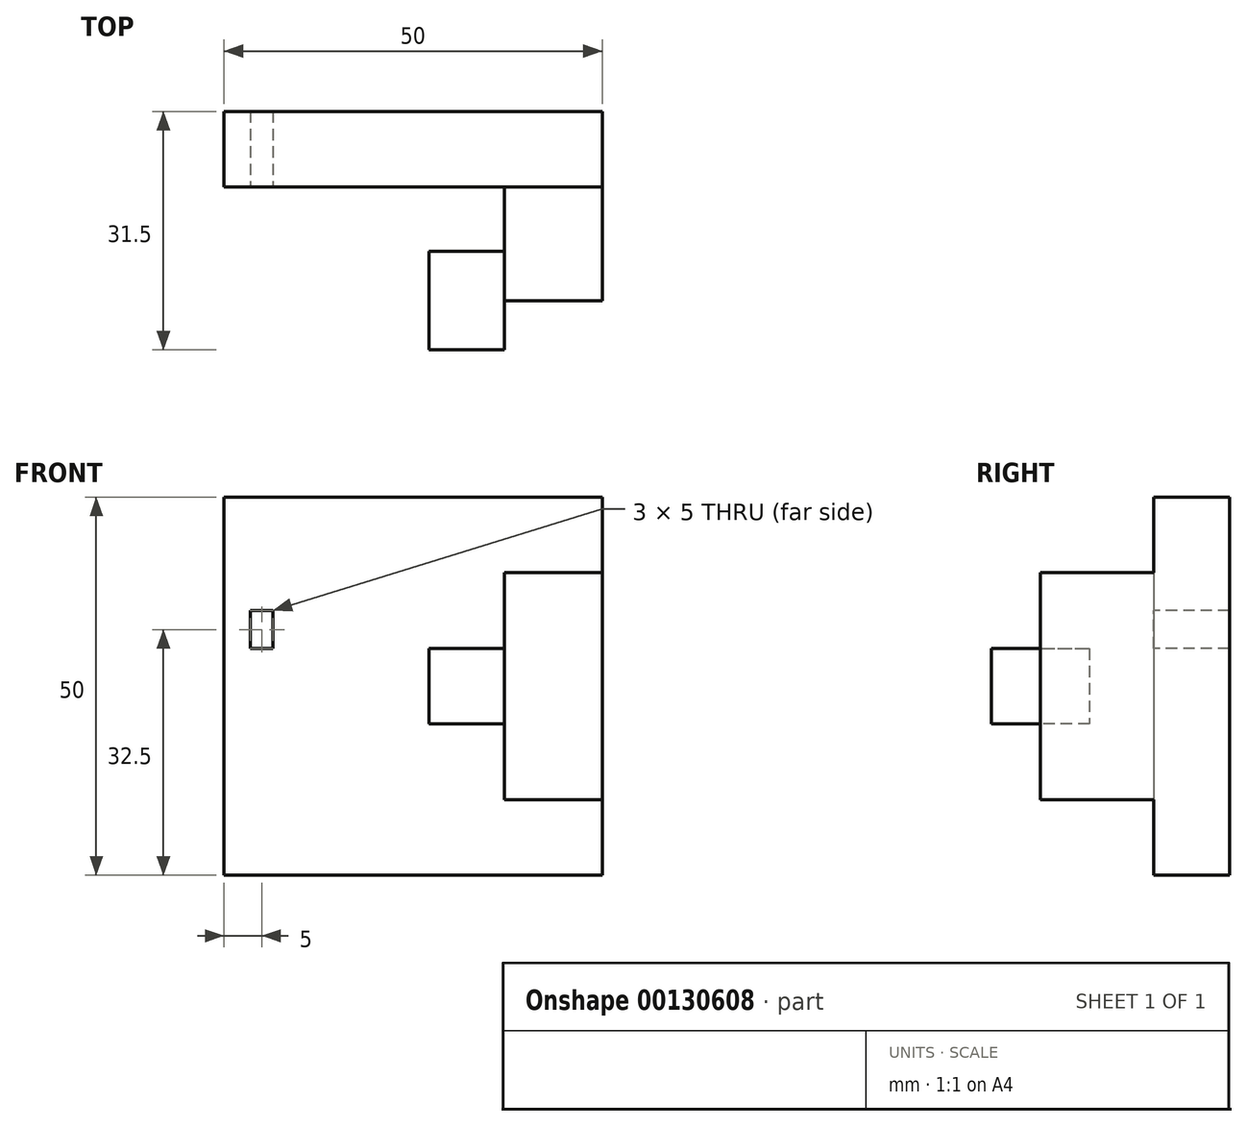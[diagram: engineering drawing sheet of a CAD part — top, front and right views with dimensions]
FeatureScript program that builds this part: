
annotation { "Feature Type Name" : "Feature", "Feature Type Description" : "" }
export const myFeature = defineFeature(function(context is Context, id is Id, definition is map)
    precondition{}
    {
        {
            var Q0;
            Q0=qCreatedBy(makeId("Front.planeOp"),FACE);
            var sketch = newSketch(context, id + "F0", { "sketchPlane" : qUnion([Q0])});
            skLineSegment(sketch, "E0.bottom", {"start": v(25, 25) * mm, "end": v(-25, 25) * mm});
            skLineSegment(sketch, "E0.top", {"start": v(25, -25) * mm, "end": v(-25, -25) * mm});
            skLineSegment(sketch, "E0.left", {"start": v(25, 25) * mm, "end": v(25, -25) * mm});
            skLineSegment(sketch, "E0.right", {"start": v(-25, 25) * mm, "end": v(-25, -25) * mm});
            skPoint(sketch, "E0.middle", {"position": v(0, 0) * mm});
            skLineSegment(sketch, "E1", {"start": v(25, 15) * mm, "end": v(12.1, 15) * mm});
            skLineSegment(sketch, "E2", {"start": v(12.1, 15) * mm, "end": v(12.1, -15) * mm});
            skLineSegment(sketch, "E3", {"start": v(12.1, -15) * mm, "end": v(25, -15) * mm});
            skLineSegment(sketch, "E4", {"start": v(-25, -15) * mm, "end": v(-12.1, -15) * mm});
            skLineSegment(sketch, "E5", {"start": v(-12.1, -15) * mm, "end": v(-12.1, 15) * mm});
            skLineSegment(sketch, "E6", {"start": v(-12.1, 15) * mm, "end": v(-25, 15) * mm});
            skSolve(sketch);
        }
        {
            var Q0;
            {var subQ0=sQuery(id+"F0.wireOp",EDGE,"E1");Q0=makeQuery(id+"F0.imprint","IMPRINT",FACE,{"disambiguationData":[TD([[makeQuery(id+"F0.imprint","IMPRINT",EDGE,{"derivedFrom":subQ0}),1.0]])]});}
            var Q1;
            {var subQ0=sQuery(id+"F0.wireOp",EDGE,"E4");Q1=makeQuery(id+"F0.imprint","IMPRINT",FACE,{"disambiguationData":[TD([[makeQuery(id+"F0.imprint","IMPRINT",EDGE,{"derivedFrom":subQ0}),1.0]])]});}
            extrude(context, id + "F1", {"entities" : qUnion([Q0, Q1]), "depth" : 25 * mm});
        }
        {
            var Q0;
            {var subQ4=sQuery(id+"F0.wireOp",EDGE,"E0.bottom");Q0=makeQuery(id+"F0.imprint","IMPRINT",FACE,{"disambiguationData":[TD([[makeQuery(id+"F0.imprint","IMPRINT",EDGE,{"derivedFrom":subQ4}),1.0]])]});}
            extrude(context, id + "F2", {"entities" : qUnion([Q0]), "operationType" : NewBodyOperationType.ADD, "depth" : 10 * mm});
        }
        {
            var Q0;
            Q0=makeQuery(id+"F1.opExtrude","SWEPT_FACE",FACE,{"disambiguationData":[OSD([sQuery(id+"F0.wireOp",EDGE,"E5")])]});
            var sketch = newSketch(context, id + "F3", { "sketchPlane" : qUnion([Q0])});
            skLineSegment(sketch, "E7", {"start": v(-25, 5) * mm, "end": v(-18.5, 5) * mm});
            skLineSegment(sketch, "E8", {"start": v(-18.5, 5) * mm, "end": v(-18.5, -5) * mm});
            skLineSegment(sketch, "E9", {"start": v(-18.5, -5) * mm, "end": v(-25, -5) * mm});
            skLineSegment(sketch, "E10", {"start": v(-10, 12.16) * mm, "end": v(-10, 1.89) * mm});
            skSolve(sketch);
        }
        {
            var Q0;
            Q0=qSketchRegion(id+"F3",true);
            var Q1;
            {var subQ0=sQuery(id+"F3.wireOp",EDGE,"E7");Q1=makeQuery(id+"F3.imprint","IMPRINT",FACE,{"disambiguationData":[TD([[makeQuery(id+"F3.imprint","IMPRINT",EDGE,{"derivedFrom":subQ0}),-1.0]])]});}
            extrude(context, id + "F4", {"entities" : qUnion([Q0, Q1]), "operationType" : NewBodyOperationType.ADD, "depth" : 10 * mm});
        }
        {
            var Q0;
            Q0=makeQuery(id+"F1.opExtrude","SWEPT_FACE",FACE,{"disambiguationData":[OSD([sQuery(id+"F0.wireOp",EDGE,"E2")])]});
            var sketch = newSketch(context, id + "F5", { "sketchPlane" : qUnion([Q0])});
            skLineSegment(sketch, "E11", {"start": v(25, 5) * mm, "end": v(18.5, 5) * mm});
            skLineSegment(sketch, "E12", {"start": v(18.5, 5) * mm, "end": v(18.5, -5) * mm});
            skLineSegment(sketch, "E13", {"start": v(18.5, -5) * mm, "end": v(25, -5) * mm});
            skSolve(sketch);
        }
        {
            var Q0;
            Q0=qSketchRegion(id+"F5",true);
            var Q1;
            {var subQ0=sQuery(id+"F5.wireOp",EDGE,"E11");Q1=makeQuery(id+"F5.imprint","IMPRINT",FACE,{"disambiguationData":[TD([[makeQuery(id+"F5.imprint","IMPRINT",EDGE,{"derivedFrom":subQ0}),1.0]])]});}
            extrude(context, id + "F6", {"entities" : qUnion([Q0, Q1]), "operationType" : NewBodyOperationType.ADD, "depth" : 10 * mm});
        }
        {
            var Q0;
            {var subQ0=sQuery(id+"F0.wireOp",EDGE,"E0.right");Q0=makeQuery(id+"F2.boolean.opBoolean","MERGE",FACE,{"derivedFrom":[makeQuery(id+"F1.opExtrude","SWEPT_FACE",FACE,{"disambiguationData":[OSD([subQ0])]}),makeQuery(id+"F2.opExtrude","SWEPT_FACE",FACE,{"disambiguationData":[OSD([subQ0]),TDD([makeQuery(id+"F0.imprint","IMPRINT",EDGE,{"disambiguationData":[TD([[makeQuery(id+"F0.imprint","INTERSECT",VERTEX,{"derivedFrom":[sQuery(id+"F0.wireOp",EDGE,"E0.bottom"),subQ0]}),-1.0]])],"derivedFrom":subQ0})])]}),makeQuery(id+"F2.opExtrude","SWEPT_FACE",FACE,{"disambiguationData":[OSD([subQ0]),TDD([makeQuery(id+"F0.imprint","IMPRINT",EDGE,{"disambiguationData":[TD([[makeQuery(id+"F0.imprint","INTERSECT",VERTEX,{"derivedFrom":[sQuery(id+"F0.wireOp",EDGE,"E0.top"),subQ0]}),1.0]])],"derivedFrom":subQ0})])]})]});}
            var sketch = newSketch(context, id + "F7", { "sketchPlane" : qUnion([Q0])});
            skLineSegment(sketch, "E14", {"start": v(10, 15) * mm, "end": v(10, -15) * mm});
            skSolve(sketch);
        }
        {
            var Q0;
            Q0 = qSketchRegion(id + "F7", true);
            var Q1;
            Q1=makeQuery(id+"F7.imprint","IMPRINT",FACE,{"disambiguationData":[TD([[makeQuery(id+"F7.imprint","IMPRINT",EDGE,{"derivedFrom":sQuery(id+"F7.wireOp",EDGE,"E14")}),1.0]])]});
            var Q2;
            Q2=makeQuery(id+"F4.opExtrude","CAP_FACE",FACE,{"disambiguationData":[OSD([sQuery(id+"F0.wireOp",EDGE,"E5"),sQuery(id+"F3.wireOp",EDGE,"E7"),sQuery(id+"F3.wireOp",EDGE,"E8"),sQuery(id+"F3.wireOp",EDGE,"E9")])],"isStart":false});
            extrude(context, id + "F8", {"entities" : qUnion([Q0, Q1]), "operationType" : NewBodyOperationType.REMOVE, "endBound" : BoundingType.UP_TO_SURFACE, "oppositeDirection" : true, "endBoundEntityFace" : qUnion([Q2]), "depth" : 25 * mm});
        }
        {
            var Q0;
            {var subQ0=sQuery(id+"F0.wireOp",EDGE,"E2");Q0=makeQuery(id+"F6.boolean.opBoolean","MERGE",FACE,{"derivedFrom":[makeQuery(id+"F1.opExtrude","CAP_FACE",FACE,{"disambiguationData":[OSD([sQuery(id+"F0.wireOp",EDGE,"E0.left"),sQuery(id+"F0.wireOp",EDGE,"E1"),subQ0,sQuery(id+"F0.wireOp",EDGE,"E3")])],"isStart":false}),makeQuery(id+"F6.opExtrude","SWEPT_FACE",FACE,{"disambiguationData":[OSD([subQ0])]})]});}
            var sketch = newSketch(context, id + "F9", { "sketchPlane" : qUnion([Q0])});
            skLineSegment(sketch, "E15", {"start": v(12.1, 5) * mm, "end": v(12.1, -5) * mm});
            skSolve(sketch);
        }
        {
            var Q0;
            Q0 = qSketchRegion(id + "F9", true);
            var Q1;
            Q1=makeQuery(id+"F9.imprint","IMPRINT",FACE,{"disambiguationData":[TD([[makeQuery(id+"F9.imprint","IMPRINT",EDGE,{"derivedFrom":sQuery(id+"F9.wireOp",EDGE,"E15")}),-1.0]])]});
            var Q2;
            Q2=makeQuery(id+"F8.boolean.opBoolean","MERGE",FACE,{"derivedFrom":[makeQuery(id+"F2.opExtrude","CAP_FACE",FACE,{"disambiguationData":[OSD([sQuery(id+"F0.wireOp",EDGE,"E0.bottom"),sQuery(id+"F0.wireOp",EDGE,"E0.top"),sQuery(id+"F0.wireOp",EDGE,"E0.left"),sQuery(id+"F0.wireOp",EDGE,"E0.right"),sQuery(id+"F0.wireOp",EDGE,"E1"),sQuery(id+"F0.wireOp",EDGE,"E2"),sQuery(id+"F0.wireOp",EDGE,"E3"),sQuery(id+"F0.wireOp",EDGE,"E4"),sQuery(id+"F0.wireOp",EDGE,"E5"),sQuery(id+"F0.wireOp",EDGE,"E6")])],"isStart":false}),makeQuery(id+"F8.opExtrude","SWEPT_FACE",FACE,{"disambiguationData":[OSD([sQuery(id+"F7.wireOp",EDGE,"E14")])]})]});
            extrude(context, id + "F10", {"entities" : qUnion([Q0, Q1]), "operationType" : NewBodyOperationType.ADD, "endBoundEntityFace" : qUnion([Q2]), "depth" : 6.5 * mm});
        }
        {
            var Q0;
            Q0=makeQuery(id+"F8.boolean.opBoolean","MERGE",FACE,{"derivedFrom":[makeQuery(id+"F2.opExtrude","CAP_FACE",FACE,{"disambiguationData":[OSD([sQuery(id+"F0.wireOp",EDGE,"E0.bottom"),sQuery(id+"F0.wireOp",EDGE,"E0.top"),sQuery(id+"F0.wireOp",EDGE,"E0.left"),sQuery(id+"F0.wireOp",EDGE,"E0.right"),sQuery(id+"F0.wireOp",EDGE,"E1"),sQuery(id+"F0.wireOp",EDGE,"E2"),sQuery(id+"F0.wireOp",EDGE,"E3"),sQuery(id+"F0.wireOp",EDGE,"E4"),sQuery(id+"F0.wireOp",EDGE,"E5"),sQuery(id+"F0.wireOp",EDGE,"E6")])],"isStart":false}),makeQuery(id+"F8.opExtrude","SWEPT_FACE",FACE,{"disambiguationData":[OSD([sQuery(id+"F7.wireOp",EDGE,"E14")])]})]});
            var sketch = newSketch(context, id + "F11", { "sketchPlane" : qUnion([Q0])});
            skLineSegment(sketch, "E16.bottom", {"start": v(-18.5, 5) * mm, "end": v(-21.5, 5) * mm});
            skLineSegment(sketch, "E16.top", {"start": v(-18.5, 10) * mm, "end": v(-21.5, 10) * mm});
            skLineSegment(sketch, "E16.left", {"start": v(-18.5, 5) * mm, "end": v(-18.5, 10) * mm});
            skLineSegment(sketch, "E16.right", {"start": v(-21.5, 5) * mm, "end": v(-21.5, 10) * mm});
            skPoint(sketch, "E16.middle", {"position": v(-20, 7.5) * mm});
            skSolve(sketch);
        }
        {
            var Q0;
            Q0=makeQuery(id+"F11.imprint","IMPRINT",FACE,{"disambiguationData":[TD([[makeQuery(id+"F11.imprint","IMPRINT",EDGE,{"derivedFrom":sQuery(id+"F11.wireOp",EDGE,"E16.bottom")}),-1.0]])]});
            extrude(context, id + "F12", {"entities" : qUnion([Q0]), "operationType" : NewBodyOperationType.REMOVE, "oppositeDirection" : true, "depth" : 10 * mm});
        }
    });
